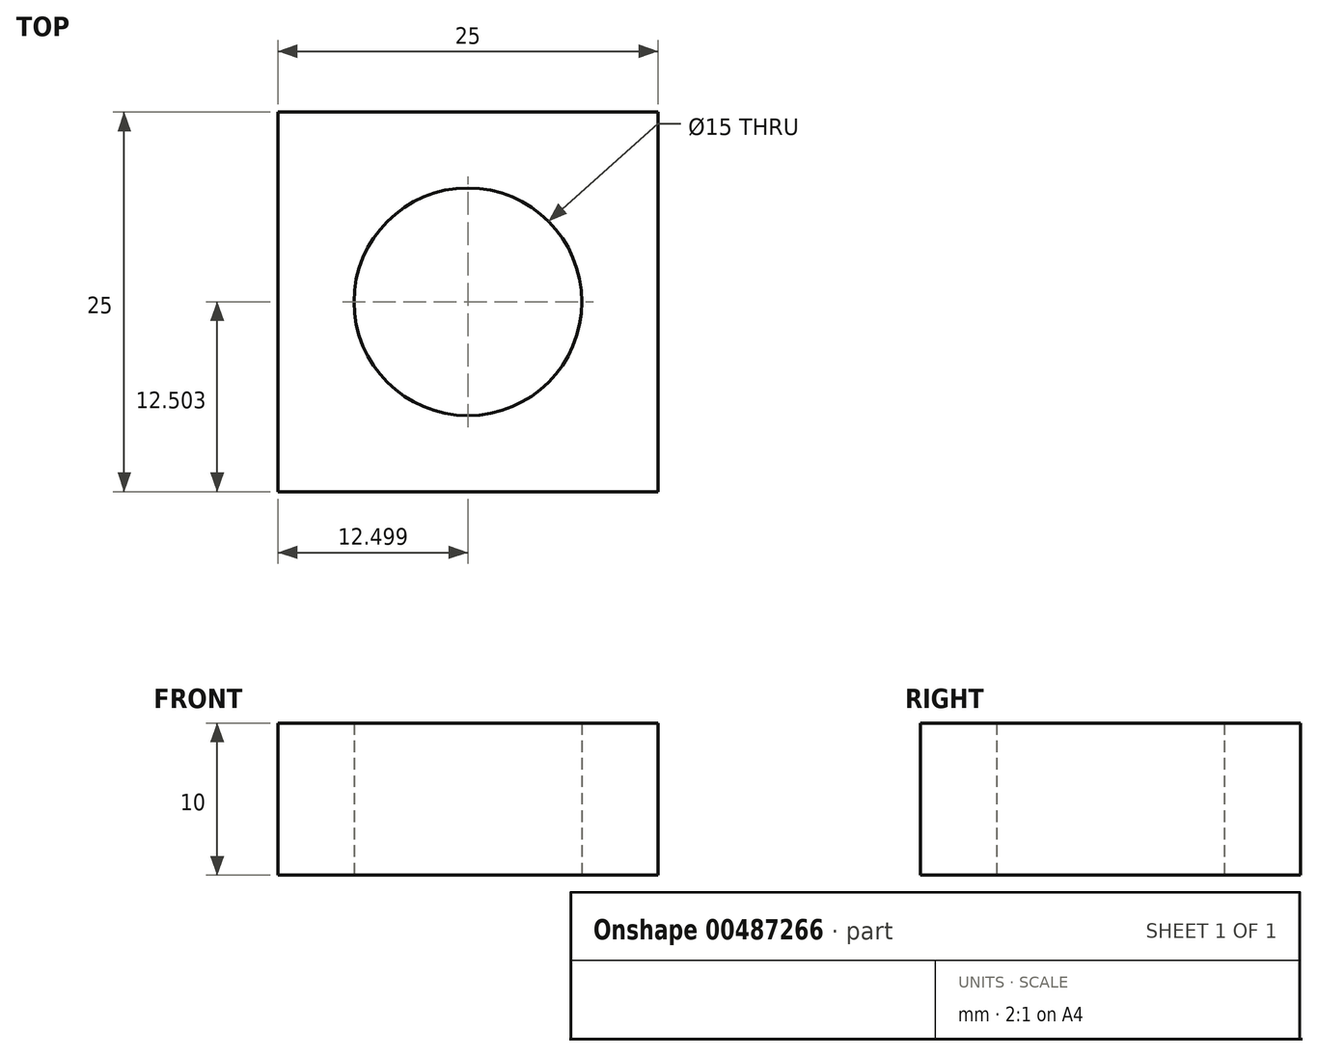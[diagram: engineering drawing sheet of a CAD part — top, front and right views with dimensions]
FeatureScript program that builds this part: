
annotation { "Feature Type Name" : "Feature", "Feature Type Description" : "" }
export const myFeature = defineFeature(function(context is Context, id is Id, definition is map)
    precondition{}
    {
        {
            var Q0;
            Q0=qCreatedBy(makeId("Top.planeOp"),FACE);
            var sketch = newSketch(context, id + "F0", { "sketchPlane" : qUnion([Q0])});
            skLineSegment(sketch, "E0.bottom", {"start": v(-9.15, -22.3) * mm, "end": v(15.85, -22.3) * mm});
            skLineSegment(sketch, "E0.top", {"start": v(-9.15, 2.7) * mm, "end": v(15.85, 2.7) * mm});
            skLineSegment(sketch, "E0.left", {"start": v(-9.15, -22.3) * mm, "end": v(-9.15, 2.7) * mm});
            skLineSegment(sketch, "E0.right", {"start": v(15.85, -22.3) * mm, "end": v(15.85, 2.7) * mm});
            skSolve(sketch);
        }
        {
            var Q0;
            Q0=makeQuery(id+"F0.imprint","IMPRINT",FACE,{"disambiguationData":[TD([[makeQuery(id+"F0.imprint","IMPRINT",EDGE,{"derivedFrom":sQuery(id+"F0.wireOp",EDGE,"E0.bottom")}),1.0]])]});
            extrude(context, id + "F1", {"entities" : qUnion([Q0]), "depth" : 10 * mm});
        }
        {
            var Q0;
            Q0=makeQuery(id+"F1.opExtrude","CAP_FACE",FACE,{"disambiguationData":[OSD([sQuery(id+"F0.wireOp",EDGE,"E0.bottom"),sQuery(id+"F0.wireOp",EDGE,"E0.top"),sQuery(id+"F0.wireOp",EDGE,"E0.left"),sQuery(id+"F0.wireOp",EDGE,"E0.right")])],"isStart":true});
            var sketch = newSketch(context, id + "F2", { "sketchPlane" : qUnion([Q0])});
            skCircle(sketch, "E1", {"center": v(3.35, 9.8) * mm, "radius": 7.5 * mm});
            skPoint(sketch, "E1.centerSnap0", {"position": v(3.35, 22.3) * mm});
            skPoint(sketch, "E1.centerSnap1", {"position": v(15.85, 9.8) * mm});
            skSolve(sketch);
        }
        {
            var Q0;
            Q0=makeQuery(id+"F2.imprint","IMPRINT",FACE,{"disambiguationData":[TD([[makeQuery(id+"F2.imprint","IMPRINT",EDGE,{"derivedFrom":sQuery(id+"F2.wireOp",EDGE,"E1")}),1.0]])]});
            extrude(context, id + "F3", {"entities" : qUnion([Q0]), "operationType" : NewBodyOperationType.REMOVE, "endBound" : BoundingType.THROUGH_ALL, "oppositeDirection" : true, "depth" : 25 * mm});
        }
    });
